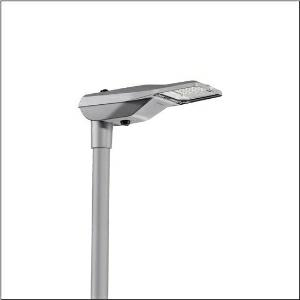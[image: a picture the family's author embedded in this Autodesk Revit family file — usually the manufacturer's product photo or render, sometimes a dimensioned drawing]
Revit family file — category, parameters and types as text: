
# Revit family: streetlight_sl_21_iq_micro___st0_8a_5xe1c31y08db_8273
name_source: partatom
category: Lighting Fixtures
units: mm (PartAtom-declared; Revit-internal decimal feet)

## family parameters
Cut with Voids When Loaded = No
Host = Face
Light Source = No
Part Type = Normal
Room Calculation Point = No
Round Connector Dimension = Use Diameter
Shared = No

## types (1)
- --- (1 x LED, 5110 lm, 39.1 W, 3000K)
    Apparent Load = 39 VA
    CIE Flux Codes = 38 75 97 100 100
    Color Rendering = 70
    Color Temperature = 3000K
    Default Elevation = 1800 mm
    Description = Streetlight SL 21 iQ micro, mast luminaire, primary light control with lens, of PMMA, primary optical cover: cover, of toughened safety glass, transparent, light distribution: ST0.8a, light emission: direct distribution, primary light characteristic: asymmetric, installation type: post-top, side-entry, LED, High Power LED, rated luminous flux: 5.110lm, luminous efficacy: 131lm/W, light colour: 730, colour temperature: 3000K, control gear: iQ-Street Remote, D4i with power reduction, control: pre-setting: logarithmic dimming characteristic, Street-Remote, Auto-Match, Temp-Guard, Lumen-Switch, Night-Set, Smart-Wire, Light-Fading, Desk-Remote (wireless, voltage-free reading and setting of iQ features in the workshop via application-optimized NFC function/RFID function), optimised constant luminous flux control (CLO 2.0), mains connection: 220..240V, AC, 50/60Hz, start of lifetime: 39W, end of service life: 41W, reduction: 17W, luminaire housing, of diecast aluminium, powder-coated, Siteco® metallic grey (DB 702S), corrosivity category C5 mid according to DIN EN ISO 12944, please order mast flange separately, inclination adjustable: 0°, 5°, 10°, 15°, sealing non-destructively replaceable, multi-level sealing system, length: 528mm, width: 235mm, height: 110mm, mast flange for spigot size: 42mm (side-entry): 5XC10008XM4, 60/48mm (side-entry/post-top): 5XC10108XM2, 76/60mm (side-entry/post-top): 5XC10108XM1, mounting height: 4..8m, Smart Interface below and above, protection rating (complete): IP66, insulation class (complete): insulation class II (safety insulation), certification: CE, ENEC, ENEC+, VDE, impact resistance: IK10, permissible operating ambient temperature for outdoor applications: -40..+50°C, standard-compliant lighting for roads and squares, packaging unit: 1 piece

Light Distribution: ST0.8a
    Height = 110 mm
    Lamp = 1 x LED
    Lamp Light Flux = 5110 lm
    Lamp Power = 39.1 W
    Lamp count = 1
    Length = 528 mm
    Luminous efficacy = 131 lm/W
    Manufacturer = Siteco
    ModVariant = No
    Model = 5XE1C31Y08DB
    Number of Poles = 1
    OnlyDefault = Yes
    Power Factor = 1
    Product Name = Streetlight SL 21 iQ micro | ST0.8a
    Product group = mast luminaire | pylon top
    ProductGroupID = 6100
    Protection Class = Protection class II
    Protection Degree = IP 66
    RLX_Detail_Level = 1
    RLX_Emergency_Light_Flux = 0 lm
    RLX_Emergency_Type = 0
    RLX_Emergency_Type_DB = No
    RlxData = <blob elided: 98785 chars, md5=362f7ab6>
    Socket = socket
    Standby Power = 0 W
    System Light Flux = 5110 lm
    System Power = 39 W
    Type Comments = factory setting: luminous flux: 100 % | dim-lin: 254 | 765 mA
    Type Image = l_1007239.jpg
    URL = http://relux.com
    VarID = @adj_134863
    Voltage = 0 V
    Weight = 0.00 kg
    Width = 235 mm

## geometry (parser evidence)
native form markers: Blend x4, Sweep x13
no freeform markers — native parametric forms only
